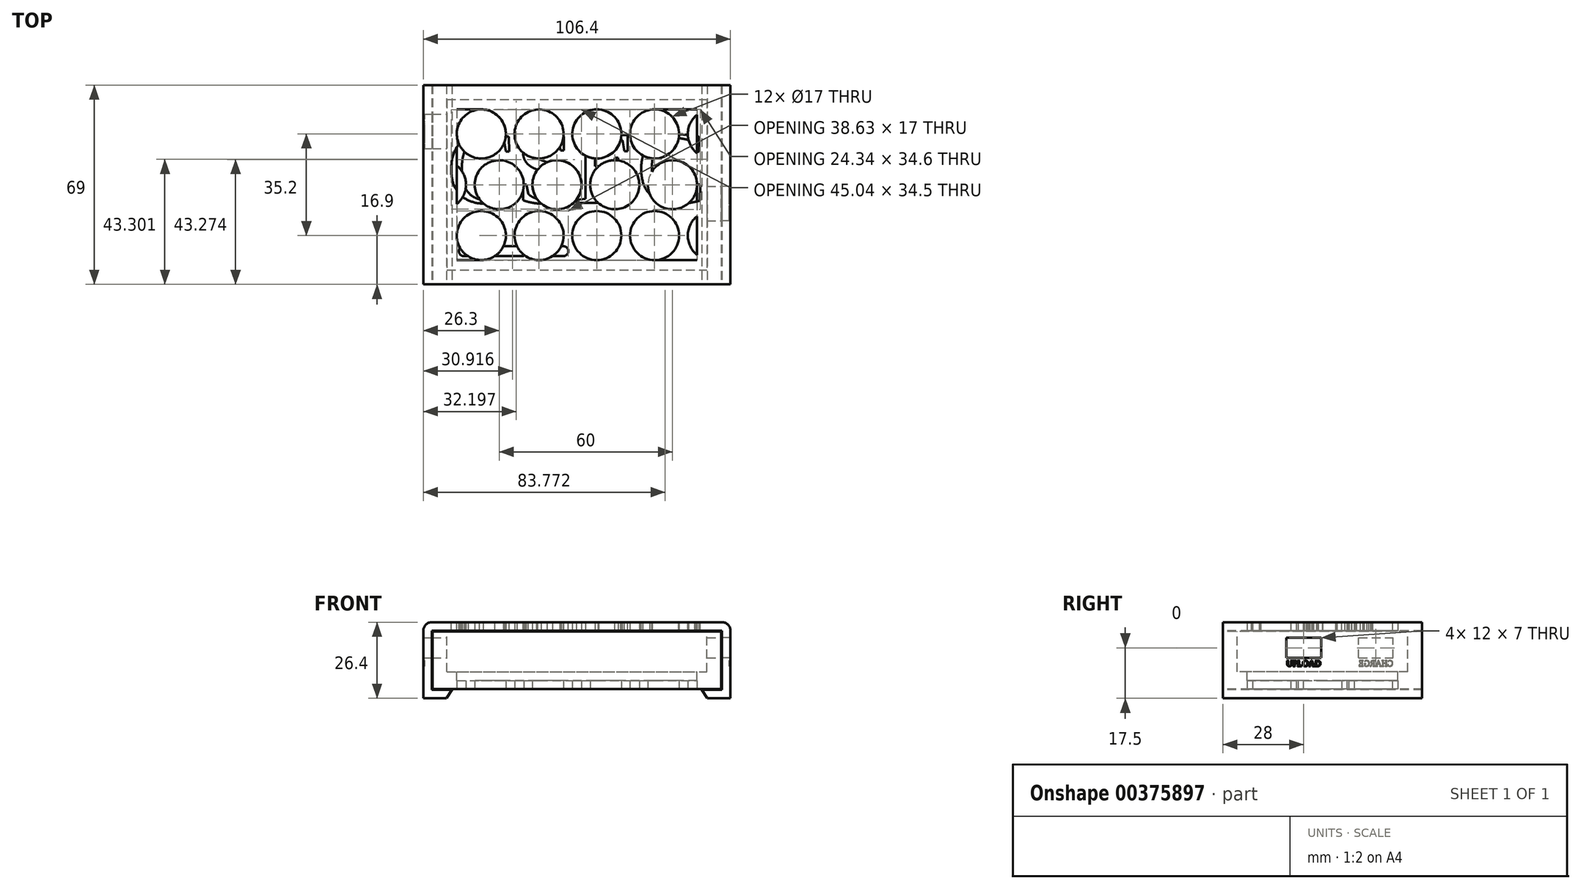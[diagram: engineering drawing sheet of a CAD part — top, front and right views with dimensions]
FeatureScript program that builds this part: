
annotation { "Feature Type Name" : "Feature", "Feature Type Description" : "" }
export const myFeature = defineFeature(function(context is Context, id is Id, definition is map)
    precondition{}
    {
        {
            var Q0;
            Q0=qCreatedBy(makeId("Top.planeOp"),FACE);
            var sketch = newSketch(context, id + "F0", { "sketchPlane" : qUnion([Q0])});
            skLineSegment(sketch, "E0.bottom", {"start": v(-50, 34.5) * mm, "end": v(50, 34.5) * mm});
            skLineSegment(sketch, "E0.top", {"start": v(-50, -34.5) * mm, "end": v(50, -34.5) * mm});
            skLineSegment(sketch, "E0.left", {"start": v(-50, 34.5) * mm, "end": v(-50, -34.5) * mm});
            skLineSegment(sketch, "E0.right", {"start": v(50, 34.5) * mm, "end": v(50, -34.5) * mm});
            skSolve(sketch);
        }
        {
            var Q0;
            Q0 = qSketchRegion(id + "F0", true);
            extrude(context, id + "F1", {"entities" : qUnion([Q0]), "depth" : 20 * mm});
        }
        {
            var Q0;
            Q0=makeQuery(id+"F1.opExtrude","CAP_FACE",FACE,{"disambiguationData":[OSD([sQuery(id+"F0.wireOp",EDGE,"E0.bottom"),sQuery(id+"F0.wireOp",EDGE,"E0.top"),sQuery(id+"F0.wireOp",EDGE,"E0.left"),sQuery(id+"F0.wireOp",EDGE,"E0.right")])],"isStart":false});
            var sketch = newSketch(context, id + "F2", { "sketchPlane" : qUnion([Q0])});
            skLineSegment(sketch, "E1.bottom", {"start": v(-45, 29.5) * mm, "end": v(45, 29.5) * mm});
            skLineSegment(sketch, "E1.top", {"start": v(-45, -29.5) * mm, "end": v(45, -29.5) * mm});
            skLineSegment(sketch, "E1.left", {"start": v(-45, 29.5) * mm, "end": v(-45, -29.5) * mm});
            skLineSegment(sketch, "E1.right", {"start": v(45, 29.5) * mm, "end": v(45, -29.5) * mm});
            skSolve(sketch);
        }
        {
            var Q0;
            Q0=makeQuery(id+"F2.imprint","IMPRINT",FACE,{"disambiguationData":[TD([[makeQuery(id+"F2.imprint","IMPRINT",EDGE,{"derivedFrom":sQuery(id+"F2.wireOp",EDGE,"E1.bottom")}),-1.0]])]});
            extrude(context, id + "F3", {"entities" : qUnion([Q0]), "operationType" : NewBodyOperationType.REMOVE, "oppositeDirection" : true, "depth" : 14 * mm});
        }
        {
            var Q0;
            Q0=makeQuery(id+"F3.boolean.opBoolean","COPY",FACE,{"derivedFrom":makeQuery(id+"F3.opExtrude","CAP_FACE",FACE,{"disambiguationData":[OSD([sQuery(id+"F2.wireOp",EDGE,"E1.bottom"),sQuery(id+"F2.wireOp",EDGE,"E1.top"),sQuery(id+"F2.wireOp",EDGE,"E1.left"),sQuery(id+"F2.wireOp",EDGE,"E1.right")])],"isStart":false})});
            var sketch = newSketch(context, id + "F4", { "sketchPlane" : qUnion([Q0])});
            skLineSegment(sketch, "E2.bottom", {"start": v(-41.6, 26.1) * mm, "end": v(41.6, 26.1) * mm});
            skLineSegment(sketch, "E2.top", {"start": v(-41.6, -26.1) * mm, "end": v(41.6, -26.1) * mm});
            skLineSegment(sketch, "E2.left", {"start": v(-41.6, 26.1) * mm, "end": v(-41.6, -26.1) * mm});
            skLineSegment(sketch, "E2.right", {"start": v(41.6, 26.1) * mm, "end": v(41.6, -26.1) * mm});
            skSolve(sketch);
        }
        {
            var Q0;
            Q0 = qSketchRegion(id + "F4", true);
            extrude(context, id + "F5", {"entities" : qUnion([Q0]), "operationType" : NewBodyOperationType.REMOVE, "oppositeDirection" : true, "depth" : 3 * mm});
        }
        {
            var Q0;
            Q0=makeQuery(id+"F1.opExtrude","SWEPT_FACE",FACE,{"disambiguationData":[OSD([sQuery(id+"F0.wireOp",EDGE,"E0.top")])]});
            cPlane(context, id + "F6", {"entities" : qUnion([Q0]), "cplaneType" : CPlaneType.OFFSET, "offset" : 0 * mm, "width" : 150 * mm, "height" : 150 * mm});
        }
        {
            var Q0;
            Q0=qCreatedBy(id+"F6.planeOp",FACE);
            var sketch = newSketch(context, id + "F7", { "sketchPlane" : qUnion([Q0])});
            skLineSegment(sketch, "E3.0.0", {"start": v(-50, 0) * mm, "end": v(50, 0) * mm});
            skLineSegment(sketch, "E3.0.1", {"start": v(50, 0) * mm, "end": v(50, 20) * mm});
            skLineSegment(sketch, "E3.0.2", {"start": v(50, 20) * mm, "end": v(-50, 20) * mm});
            skLineSegment(sketch, "E3.0.3", {"start": v(-50, 20) * mm, "end": v(-50, 0) * mm});
            skLineSegment(sketch, "E4", {"start": v(0, 23.2) * mm, "end": v(-53.2, 23.2) * mm});
            skLineSegment(sketch, "E5", {"start": v(-53.2, 23.2) * mm, "end": v(-53.2, -3.2) * mm});
            skLineSegment(sketch, "E6", {"start": v(-53.2, -3.2) * mm, "end": v(-45.2, -3.2) * mm});
            skLineSegment(sketch, "E7", {"start": v(-45.2, -3.2) * mm, "end": v(-43.2, -0.2) * mm});
            skLineSegment(sketch, "E8", {"start": v(-43.2, -0.2) * mm, "end": v(-50.2, -0.2) * mm});
            skLineSegment(sketch, "E9", {"start": v(-50.2, -0.2) * mm, "end": v(-50.2, 20.2) * mm});
            skLineSegment(sketch, "E10", {"start": v(-50.2, 20.2) * mm, "end": v(0, 20.2) * mm});
            skLineSegment(sketch, "E11", {"start": v(0, 20.2) * mm, "end": v(0, 23.2) * mm});
            skLineSegment(sketch, "E12.MirrorCS", {"start": v(0, 23.2) * mm, "end": v(53.2, 23.2) * mm});
            skLineSegment(sketch, "E13.MirrorCS", {"start": v(50.2, 20.2) * mm, "end": v(0, 20.2) * mm});
            skLineSegment(sketch, "E14.MirrorCS", {"start": v(53.2, 23.2) * mm, "end": v(53.2, -3.2) * mm});
            skLineSegment(sketch, "E15.MirrorCS", {"start": v(50.2, -0.2) * mm, "end": v(50.2, 20.2) * mm});
            skLineSegment(sketch, "E16.MirrorCS", {"start": v(53.2, -3.2) * mm, "end": v(45.2, -3.2) * mm});
            skLineSegment(sketch, "E17.MirrorCS", {"start": v(45.2, -3.2) * mm, "end": v(43.2, -0.2) * mm});
            skLineSegment(sketch, "E18.MirrorCS", {"start": v(43.2, -0.2) * mm, "end": v(50.2, -0.2) * mm});
            skSolve(sketch);
        }
        {
            var Q0;
            Q0=makeQuery(id+"F7.imprint","IMPRINT",FACE,{"disambiguationData":[TD([[makeQuery(id+"F7.imprint","IMPRINT",EDGE,{"derivedFrom":sQuery(id+"F7.wireOp",EDGE,"E4")}),1.0]])]});
            var Q1;
            Q1=makeQuery(id+"F7.imprint","IMPRINT",FACE,{"disambiguationData":[TD([[makeQuery(id+"F7.imprint","IMPRINT",EDGE,{"derivedFrom":sQuery(id+"F7.wireOp",EDGE,"E11")}),-1.0]])]});
            extrude(context, id + "F8", {"entities" : qUnion([Q0, Q1]), "oppositeDirection" : true, "depth" : 69 * mm});
        }
        {
            var Q0;
            Q0=makeQuery(id+"F8.opExtrude","SWEPT_FACE",FACE,{"disambiguationData":[OSD([sQuery(id+"F7.wireOp",EDGE,"E4"),sQuery(id+"F7.wireOp",EDGE,"E12.MirrorCS")])]});
            var sketch = newSketch(context, id + "F9", { "sketchPlane" : qUnion([Q0])});
            skLineSegment(sketch, "E19.bottom", {"start": v(-39.1, -21.25) * mm, "end": v(-19.1, -21.25) * mm});
            skLineSegment(sketch, "E19.top", {"start": v(-39.1, -24.75) * mm, "end": v(-19.1, -24.75) * mm});
            skLineSegment(sketch, "E19.left", {"start": v(-39.1, -21.25) * mm, "end": v(-39.1, -24.75) * mm});
            skLineSegment(sketch, "E19.right", {"start": v(-19.1, -21.25) * mm, "end": v(-19.1, -24.75) * mm});
            skArc(sketch, "E20", {"start": v(-39.1, -21.25) * mm, "mid": v(-40.84, -23) * mm, "end": v(-39.1, -24.75) * mm});
            skArc(sketch, "E21", {"start": v(-19.1, -24.75) * mm, "mid": v(-17.34, -23) * mm, "end": v(-19.1, -21.25) * mm});
            skLineSegment(sketch, "E22", {"start": v(-19.1, -21.25) * mm, "end": v(-4.03, -21.25) * mm, "construction": true});
            skLineSegment(sketch, "E23", {"start": v(-19.1, -24.75) * mm, "end": v(-4.03, -24.75) * mm, "construction": true});
            skLineSegment(sketch, "E24.bottom", {"start": v(-14.72, -21.25) * mm, "end": v(-4.72, -21.25) * mm});
            skLineSegment(sketch, "E24.top", {"start": v(-14.72, -24.75) * mm, "end": v(-4.72, -24.75) * mm});
            skLineSegment(sketch, "E24.left", {"start": v(-14.72, -21.25) * mm, "end": v(-14.72, -24.75) * mm});
            skLineSegment(sketch, "E24.right", {"start": v(-4.72, -21.25) * mm, "end": v(-4.72, -24.75) * mm});
            skArc(sketch, "E25", {"start": v(-14.72, -21.25) * mm, "mid": v(-16.47, -23) * mm, "end": v(-14.72, -24.75) * mm});
            skArc(sketch, "E26", {"start": v(-4.72, -24.75) * mm, "mid": v(-2.97, -23) * mm, "end": v(-4.72, -21.25) * mm});
            skSolve(sketch);
        }
        {
            var Q0;
            Q0 = qSketchRegion(id + "F9", true);
            extrude(context, id + "F10", {"entities" : qUnion([Q0]), "operationType" : NewBodyOperationType.REMOVE, "oppositeDirection" : true, "depth" : 5 * mm});
        }
        {
            var Q0;
            Q0=makeQuery(id+"F1.opExtrude","CAP_FACE",FACE,{"disambiguationData":[OSD([sQuery(id+"F0.wireOp",EDGE,"E0.bottom"),sQuery(id+"F0.wireOp",EDGE,"E0.top"),sQuery(id+"F0.wireOp",EDGE,"E0.left"),sQuery(id+"F0.wireOp",EDGE,"E0.right")])],"isStart":true});
            var sketch = newSketch(context, id + "F11", { "sketchPlane" : qUnion([Q0])});
            skLineSegment(sketch, "E27.0", {"start": v(-41.6, -26.1) * mm, "end": v(-41.6, 26.1) * mm});
            skLineSegment(sketch, "E28.0", {"start": v(-41.6, -26.1) * mm, "end": v(41.6, -26.1) * mm});
            skLineSegment(sketch, "E29.0", {"start": v(41.6, -26.1) * mm, "end": v(41.6, 26.1) * mm});
            skLineSegment(sketch, "E30.0", {"start": v(-41.6, 26.1) * mm, "end": v(41.6, 26.1) * mm});
            skCircle(sketch, "E31", {"center": v(-33.1, 17.6) * mm, "radius": 8.5 * mm});
            skCircle(sketch, "E32.1.0.0", {"center": v(-13.1, 17.6) * mm, "radius": 8.5 * mm});
            skCircle(sketch, "E32.2.0.0", {"center": v(6.9, 17.6) * mm, "radius": 8.5 * mm});
            skCircle(sketch, "E32.3.0.0", {"center": v(26.9, 17.6) * mm, "radius": 8.5 * mm});
            skArc(sketch, "E32.4.0.0", {"start": v(41.6, 24.25) * mm, "mid": v(38.4, 17.6) * mm, "end": v(41.6, 10.95) * mm});
            skLineSegment(sketch, "E32.direction1", {"start": v(-33.1, 17.6) * mm, "end": v(-13.1, 17.6) * mm, "construction": true});
            skCircle(sketch, "E33", {"center": v(33.1, 0) * mm, "radius": 8.5 * mm});
            skCircle(sketch, "E34.1.0.0", {"center": v(13.1, 0) * mm, "radius": 8.5 * mm});
            skCircle(sketch, "E34.2.0.0", {"center": v(-6.9, 0) * mm, "radius": 8.5 * mm});
            skCircle(sketch, "E34.3.0.0", {"center": v(-26.9, 0) * mm, "radius": 8.5 * mm});
            skArc(sketch, "E34.4.0.0", {"start": v(-41.6, -6.65) * mm, "mid": v(-38.4, 0) * mm, "end": v(-41.6, 6.65) * mm});
            skLineSegment(sketch, "E34.direction1", {"start": v(33.1, 0) * mm, "end": v(13.1, 0) * mm, "construction": true});
            skCircle(sketch, "E35", {"center": v(-33.1, -17.6) * mm, "radius": 8.5 * mm});
            skCircle(sketch, "E36.1.0.0", {"center": v(-13.1, -17.6) * mm, "radius": 8.5 * mm});
            skCircle(sketch, "E36.2.0.0", {"center": v(6.9, -17.6) * mm, "radius": 8.5 * mm});
            skCircle(sketch, "E36.3.0.0", {"center": v(26.9, -17.6) * mm, "radius": 8.5 * mm});
            skArc(sketch, "E36.4.0.0", {"start": v(41.6, -10.95) * mm, "mid": v(38.4, -17.6) * mm, "end": v(41.6, -24.25) * mm});
            skLineSegment(sketch, "E36.direction1", {"start": v(-33.1, -17.6) * mm, "end": v(-13.1, -17.6) * mm, "construction": true});
            skSolve(sketch);
        }
        {
            var Q0;
            Q0=makeQuery(id+"F11.imprint","IMPRINT",FACE,{"disambiguationData":[TD([[makeQuery(id+"F11.imprint","IMPRINT",EDGE,{"derivedFrom":sQuery(id+"F11.wireOp",EDGE,"E32.1.0.0")}),1.0]])]});
            var Q1;
            Q1=makeQuery(id+"F11.imprint","IMPRINT",FACE,{"disambiguationData":[TD([[makeQuery(id+"F11.imprint","IMPRINT",EDGE,{"derivedFrom":sQuery(id+"F11.wireOp",EDGE,"E32.3.0.0")}),1.0]])]});
            var Q2;
            Q2=makeQuery(id+"F11.imprint","IMPRINT",FACE,{"disambiguationData":[TD([[makeQuery(id+"F11.imprint","IMPRINT",EDGE,{"derivedFrom":sQuery(id+"F11.wireOp",EDGE,"E36.1.0.0")}),1.0]])]});
            var Q3;
            Q3=makeQuery(id+"F11.imprint","IMPRINT",FACE,{"disambiguationData":[TD([[makeQuery(id+"F11.imprint","IMPRINT",EDGE,{"derivedFrom":sQuery(id+"F11.wireOp",EDGE,"E36.2.0.0")}),1.0]])]});
            var Q4;
            Q4=makeQuery(id+"F11.imprint","IMPRINT",FACE,{"disambiguationData":[TD([[makeQuery(id+"F11.imprint","IMPRINT",EDGE,{"derivedFrom":sQuery(id+"F11.wireOp",EDGE,"E36.3.0.0")}),1.0]])]});
            var Q5;
            {var subQ0=sQuery(id+"F11.wireOp",EDGE,"E34.4.0.0");Q5=makeQuery(id+"F11.imprint","IMPRINT",FACE,{"disambiguationData":[TD([[makeQuery(id+"F11.imprint","IMPRINT",EDGE,{"derivedFrom":subQ0}),1.0]])]});}
            var Q6;
            {var subQ0=sQuery(id+"F11.wireOp",EDGE,"E36.4.0.0");Q6=makeQuery(id+"F11.imprint","IMPRINT",FACE,{"disambiguationData":[TD([[makeQuery(id+"F11.imprint","IMPRINT",EDGE,{"derivedFrom":subQ0}),1.0]])]});}
            var Q7;
            {var subQ0=sQuery(id+"F11.wireOp",EDGE,"E32.4.0.0");Q7=makeQuery(id+"F11.imprint","IMPRINT",FACE,{"disambiguationData":[TD([[makeQuery(id+"F11.imprint","IMPRINT",EDGE,{"derivedFrom":subQ0}),1.0]])]});}
            var Q8;
            {var subQ0=sQuery(id+"F11.wireOp",EDGE,"E31");var subQ1=makeQuery(id+"F11.imprint","INTERSECT",VERTEX,{"derivedFrom":[sQuery(id+"F11.wireOp",EDGE,"E27.0"),subQ0]});Q8=makeQuery(id+"F11.imprint","IMPRINT",FACE,{"disambiguationData":[TD([[makeQuery(id+"F11.imprint","IMPRINT",EDGE,{"disambiguationData":[TD([[subQ1,1.0]])],"derivedFrom":subQ0}),1.0]])]});}
            var Q9;
            {var subQ0=sQuery(id+"F11.wireOp",EDGE,"E35");var subQ1=makeQuery(id+"F11.imprint","INTERSECT",VERTEX,{"derivedFrom":[sQuery(id+"F11.wireOp",EDGE,"E27.0"),subQ0]});Q9=makeQuery(id+"F11.imprint","IMPRINT",FACE,{"disambiguationData":[TD([[makeQuery(id+"F11.imprint","IMPRINT",EDGE,{"disambiguationData":[TD([[subQ1,-1.0]])],"derivedFrom":subQ0}),1.0]])]});}
            var Q10;
            Q10=makeQuery(id+"F11.imprint","IMPRINT",FACE,{"disambiguationData":[TD([[makeQuery(id+"F11.imprint","IMPRINT",EDGE,{"derivedFrom":sQuery(id+"F11.wireOp",EDGE,"E34.2.0.0")}),1.0]])]});
            var Q11;
            Q11=makeQuery(id+"F11.imprint","IMPRINT",FACE,{"disambiguationData":[TD([[makeQuery(id+"F11.imprint","IMPRINT",EDGE,{"derivedFrom":sQuery(id+"F11.wireOp",EDGE,"E34.1.0.0")}),1.0]])]});
            var Q12;
            Q12=makeQuery(id+"F11.imprint","IMPRINT",FACE,{"disambiguationData":[TD([[makeQuery(id+"F11.imprint","IMPRINT",EDGE,{"derivedFrom":sQuery(id+"F11.wireOp",EDGE,"E34.3.0.0")}),1.0]])]});
            var Q13;
            Q13=makeQuery(id+"F11.imprint","IMPRINT",FACE,{"disambiguationData":[TD([[makeQuery(id+"F11.imprint","IMPRINT",EDGE,{"derivedFrom":sQuery(id+"F11.wireOp",EDGE,"E33")}),1.0]])]});
            var Q14;
            Q14=makeQuery(id+"F11.imprint","IMPRINT",FACE,{"disambiguationData":[TD([[makeQuery(id+"F11.imprint","IMPRINT",EDGE,{"derivedFrom":sQuery(id+"F11.wireOp",EDGE,"E32.2.0.0")}),1.0]])]});
            extrude(context, id + "F12", {"entities" : qUnion([Q0, Q1, Q2, Q3, Q4, Q5, Q6, Q7, Q8, Q9, Q10, Q11, Q12, Q13, Q14]), "operationType" : NewBodyOperationType.REMOVE, "oppositeDirection" : true, "depth" : 25 * mm});
        }
        {
            var Q0;
            Q0=makeQuery(id+"F1.opExtrude","SWEPT_FACE",FACE,{"disambiguationData":[OSD([sQuery(id+"F0.wireOp",EDGE,"E0.right")])]});
            var sketch = newSketch(context, id + "F13", { "sketchPlane" : qUnion([Q0])});
            skLineSegment(sketch, "E37.bottom", {"start": v(-12.5, 17.8) * mm, "end": v(-0.5, 17.8) * mm});
            skLineSegment(sketch, "E37.top", {"start": v(-12.5, 10.8) * mm, "end": v(-0.5, 10.8) * mm});
            skLineSegment(sketch, "E37.left", {"start": v(-12.5, 17.8) * mm, "end": v(-12.5, 10.8) * mm});
            skLineSegment(sketch, "E37.right", {"start": v(-0.5, 17.8) * mm, "end": v(-0.5, 10.8) * mm});
            skSolve(sketch);
        }
        {
            var Q0;
            Q0=makeQuery(id+"F13.imprint","IMPRINT",FACE,{"disambiguationData":[TD([[makeQuery(id+"F13.imprint","IMPRINT",EDGE,{"derivedFrom":sQuery(id+"F13.wireOp",EDGE,"E37.bottom")}),-1.0]])]});
            extrude(context, id + "F14", {"entities" : qUnion([Q0]), "operationType" : NewBodyOperationType.REMOVE, "depth" : 25 * mm});
        }
        {
            var Q0;
            Q0=makeQuery(id+"F8.opExtrude","SWEPT_FACE",FACE,{"disambiguationData":[OSD([sQuery(id+"F7.wireOp",EDGE,"E4"),sQuery(id+"F7.wireOp",EDGE,"E12.MirrorCS")])]});
            var sketch = newSketch(context, id + "F15", { "sketchPlane" : qUnion([Q0])});
            skText(sketch, "E38", { "text": "CSEC", "fontName": "Tinos-Regular.ttf"});
            const initialGuessF15  = {"E38": [-0.045, -0.00625, 1, 0, 0.02583]};
            skSetInitialGuess(sketch, initialGuessF15);
            skSolve(sketch);
        }
        {
            var Q0;
            Q0 = qSketchRegion(id + "F15", true);
            var Q1;
            Q1=makeQuery(id+"F8.opExtrude","SWEPT_FACE",FACE,{"disambiguationData":[OSD([sQuery(id+"F7.wireOp",EDGE,"E10"),sQuery(id+"F7.wireOp",EDGE,"E13.MirrorCS")])]});
            extrude(context, id + "F16", {"entities" : qUnion([Q0]), "operationType" : NewBodyOperationType.REMOVE, "endBound" : BoundingType.UP_TO_SURFACE, "oppositeDirection" : true, "endBoundEntityFace" : qUnion([Q1]), "depth" : 25 * mm});
        }
        {
            var Q0;
            Q0=makeQuery(id+"F13.imprint","IMPRINT",FACE,{"disambiguationData":[TD([[makeQuery(id+"F13.imprint","IMPRINT",EDGE,{"derivedFrom":sQuery(id+"F13.wireOp",EDGE,"E37.bottom")}),-1.0]])]});
            extrude(context, id + "F17", {"entities" : qUnion([Q0]), "operationType" : NewBodyOperationType.REMOVE, "oppositeDirection" : true, "depth" : 25 * mm});
        }
        {
            var Q0;
            Q0=makeQuery(id+"F1.opExtrude","SWEPT_FACE",FACE,{"disambiguationData":[OSD([sQuery(id+"F0.wireOp",EDGE,"E0.left")])]});
            var sketch = newSketch(context, id + "F18", { "sketchPlane" : qUnion([Q0])});
            skLineSegment(sketch, "E39.bottom", {"start": v(-24.5, 17.8) * mm, "end": v(-12.5, 17.8) * mm});
            skLineSegment(sketch, "E39.top", {"start": v(-24.5, 10.8) * mm, "end": v(-12.5, 10.8) * mm});
            skLineSegment(sketch, "E39.left", {"start": v(-24.5, 17.8) * mm, "end": v(-24.5, 10.8) * mm});
            skLineSegment(sketch, "E39.right", {"start": v(-12.5, 17.8) * mm, "end": v(-12.5, 10.8) * mm});
            skSolve(sketch);
        }
        {
            var Q0;
            Q0=makeQuery(id+"F18.imprint","IMPRINT",FACE,{"disambiguationData":[TD([[makeQuery(id+"F18.imprint","IMPRINT",EDGE,{"derivedFrom":sQuery(id+"F18.wireOp",EDGE,"E39.bottom")}),-1.0]])]});
            extrude(context, id + "F19", {"entities" : qUnion([Q0]), "operationType" : NewBodyOperationType.REMOVE, "endBound" : BoundingType.SYMMETRIC, "depth" : 25 * mm});
        }
        {
            var Q0;
            Q0=makeQuery(id+"F8.opExtrude","SWEPT_FACE",FACE,{"disambiguationData":[OSD([sQuery(id+"F7.wireOp",EDGE,"E14.MirrorCS")])]});
            var sketch = newSketch(context, id + "F20", { "sketchPlane" : qUnion([Q0])});
            skText(sketch, "E40", { "text": "UPLOAD", "fontName": "Tinos-Regular.ttf"});
            skLineSegment(sketch, "E41.0.0", {"start": v(34.5, -3.2) * mm, "end": v(34.5, 20.2) * mm});
            skLineSegment(sketch, "E41.0.1", {"start": v(34.5, 20.2) * mm, "end": v(-34.5, 20.2) * mm});
            skLineSegment(sketch, "E41.0.2", {"start": v(-34.5, 20.2) * mm, "end": v(-34.5, -3.2) * mm});
            skLineSegment(sketch, "E41.0.3", {"start": v(-34.5, -3.2) * mm, "end": v(34.5, -3.2) * mm});
            const initialGuessF20  = {"E40": [-0.0125, 0.00793, 1, 0, 0.00212]};
            skSetInitialGuess(sketch, initialGuessF20);
            skSolve(sketch);
        }
        {
            var Q0;
            Q0=makeQuery(id+"F20.imprint","IMPRINT",FACE,{"disambiguationData":[TD([[makeQuery(id+"F20.imprint","IMPRINT",EDGE,{"derivedFrom":sQuery(id+"F20.wireOp",EDGE,"E40.sketch_text.stroke-0")}),-1.0]])]});
            var Q1;
            Q1=makeQuery(id+"F20.imprint","IMPRINT",FACE,{"disambiguationData":[TD([[makeQuery(id+"F20.imprint","IMPRINT",EDGE,{"derivedFrom":sQuery(id+"F20.wireOp",EDGE,"E40.sketch_text.stroke-21")}),-1.0]])]});
            var Q2;
            Q2=makeQuery(id+"F20.imprint","IMPRINT",FACE,{"disambiguationData":[TD([[makeQuery(id+"F20.imprint","IMPRINT",EDGE,{"derivedFrom":sQuery(id+"F20.wireOp",EDGE,"E40.sketch_text.stroke-42")}),-1.0]])]});
            var Q3;
            Q3=makeQuery(id+"F20.imprint","IMPRINT",FACE,{"disambiguationData":[TD([[makeQuery(id+"F20.imprint","IMPRINT",EDGE,{"derivedFrom":sQuery(id+"F20.wireOp",EDGE,"E40.sketch_text.stroke-57")}),-1.0]])]});
            var Q4;
            Q4=makeQuery(id+"F20.imprint","IMPRINT",FACE,{"disambiguationData":[TD([[makeQuery(id+"F20.imprint","IMPRINT",EDGE,{"derivedFrom":sQuery(id+"F20.wireOp",EDGE,"E40.sketch_text.stroke-72")}),-1.0]])]});
            var Q5;
            Q5=makeQuery(id+"F20.imprint","IMPRINT",FACE,{"disambiguationData":[TD([[makeQuery(id+"F20.imprint","IMPRINT",EDGE,{"derivedFrom":sQuery(id+"F20.wireOp",EDGE,"E40.sketch_text.stroke-91")}),-1.0]])]});
            extrude(context, id + "F21", {"entities" : qUnion([Q0, Q1, Q2, Q3, Q4, Q5]), "operationType" : NewBodyOperationType.REMOVE, "oppositeDirection" : true, "depth" : 0.4 * mm});
        }
        {
            var Q0;
            Q0=makeQuery(id+"F8.opExtrude","SWEPT_FACE",FACE,{"disambiguationData":[OSD([sQuery(id+"F7.wireOp",EDGE,"E5")])]});
            var sketch = newSketch(context, id + "F22", { "sketchPlane" : qUnion([Q0])});
            skText(sketch, "E42", { "text": "CHARGE", "fontName": "Tinos-Regular.ttf"});
            const initialGuessF22  = {"E42": [-0.0245, 0.00796, 1, 0, 0.0021]};
            skSetInitialGuess(sketch, initialGuessF22);
            skSolve(sketch);
        }
        {
            var Q0;
            Q0 = qSketchRegion(id + "F22", true);
            extrude(context, id + "F23", {"entities" : qUnion([Q0]), "operationType" : NewBodyOperationType.REMOVE, "oppositeDirection" : true, "depth" : 0.4 * mm});
        }
        {
            var Q0;
            Q0=makeQuery(id+"F8.opExtrude","SWEPT_EDGE",EDGE,{"disambiguationData":[OSD([sQuery(id+"F7.wireOp",EDGE,"E4"),sQuery(id+"F7.wireOp",EDGE,"E5")])]});
            var Q1;
            Q1=makeQuery(id+"F8.opExtrude","SWEPT_EDGE",EDGE,{"disambiguationData":[OSD([sQuery(id+"F7.wireOp",EDGE,"E12.MirrorCS"),sQuery(id+"F7.wireOp",EDGE,"E14.MirrorCS")])]});
            fillet(context, id + "F24", {"entities" : qUnion([Q0, Q1]), "radius" : 3 * mm, "tangentPropagation" : true, "allowEdgeOverflow" : false});
        }
    });
